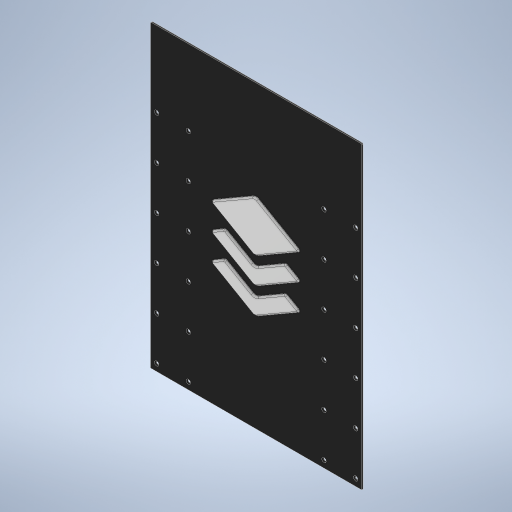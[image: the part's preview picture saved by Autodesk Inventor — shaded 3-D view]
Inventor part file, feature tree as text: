
AUTODESK INVENTOR PART (.ipt)
format: ipt  version: 2024 (Build 280153000, 153)  size: 465,920 bytes
history: native  units: mm
features: fillet x4, sketch x3, extrude x3, projected_geometry x3, hole x1, chamfer x1, other x1
ambient origin geometry x8: Origin, YZ Plane, XZ Plane, XY Plane, X Axis, Y Axis, Z Axis, Center Point
bodies: Solid1 (feature_tree)
feature tree (16):
  sketch  "Sketch1"  dims[d0=468.7mm d1=664.35mm]
  extrude  "Extrusion1"  Depth=664.35mm
  hole  "Hole1"  [1 undecoded]
  extrude  "Extrusion4"  Depth=2.0mm
  fillet  "Fillet3"  Radius=16.35mm
  fillet  "Fillet4"  Radius=16.35mm
  fillet  "Fillet2"  Radius=60.0mm
  extrude  "Extrusion5"  Depth=2.0mm
  chamfer  "Chamfer1"  Distance=220.0mm
  fillet  "Fillet5"  Radius=84.35mm
  sketch  "Sketch4"  dims[d2=3.0mm d3=0.0mm d17=512.7mm]
  sketch  "Sketch5"  dims[d25=480.0mm d26=14.35mm d27=16.35mm d28=16.35mm d29=60.0mm d31=96.0mm d32=20.0mm d34=440.0mm d37=220.0mm d38=220.0mm d39=84.35mm d40=60.0mm d42=96.0mm d43=20.0mm d45=300.0mm d48=84.35mm d49=1.0mm d50=5.4mm d51=6.0mm d52=10.0mm d53=2.0mm d54=90.0deg d55=8.0mm d56=0.0mm d57=16.666667mm d58=33.333333mm d59=16.666667mm d60=33.333333mm d61=200.0mm d62=1.5mm d63=0.0mm d64=4.0mm d65=12.0mm d69=5.0mm d70=0.0mm d71=3.0mm d72=2.0mm d73=45.0deg d74=6.0mm d75=0.25mm d76=0.25mm d77=0.25mm d78=2.0mm d79=0.0mm d80=0.0mm d81=0.0mm]
  other  "LOGO"
  projected_geometry  "Projected Loop5"
  projected_geometry  "Projected Loop6"
  projected_geometry  "Projected Loop7"
note: 1 required parameter value undecoded (feature->parameter linkage not recoverable at this tier; creation-order binding heuristic only, values carry confidence <= 0.55)
